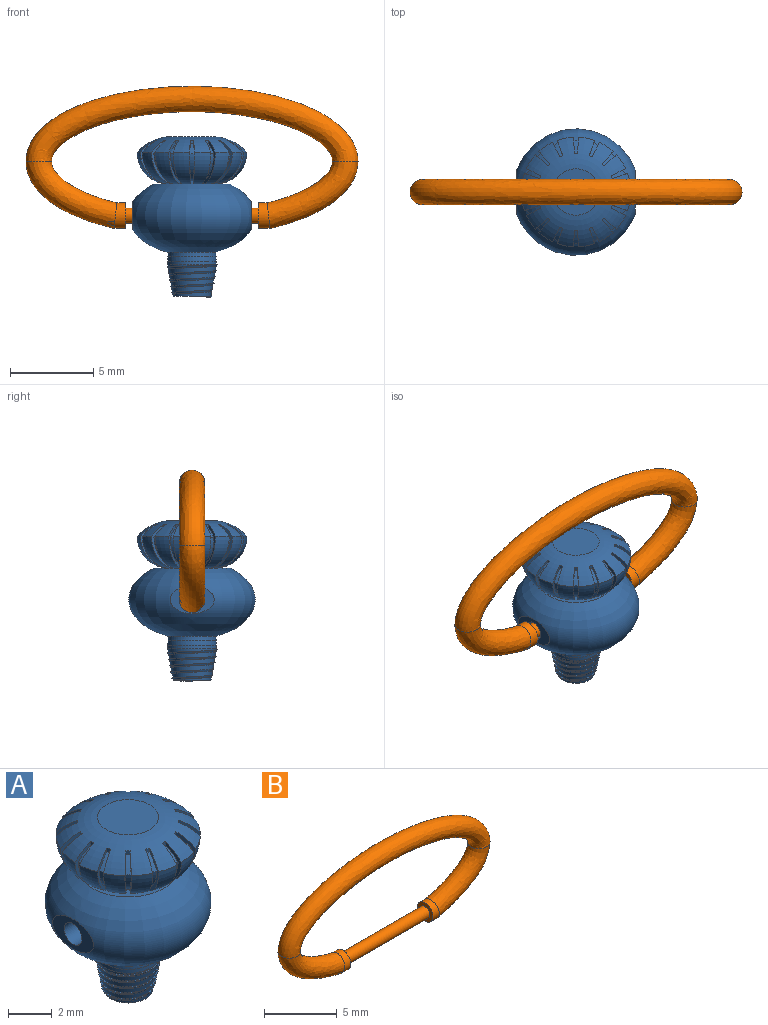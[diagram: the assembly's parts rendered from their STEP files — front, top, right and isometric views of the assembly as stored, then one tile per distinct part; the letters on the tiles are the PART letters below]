
ASSEMBLY  parts=2 mates=1
PART A: 129 faces, bbox 7.6x7.6x9.7 mm
  f0: cone r=1.13mm half-angle=10deg, axis (0,0,1), area 12.2mm2, adj f1,f3,f124,f125,f126,f127
  f1: cylinder r=1.47mm len=2.93mm, axis (0,0,-1), area 2mm2, adj f0,f4,f126,f127
  f2: revolved ~7.62x7.62mm, area 108mm2, adj f5,f6,f121,f122
  f3: plane 2.27x2.27mm, normal (0,0,-1), area 4mm2, adj f0,f124,f125
  f4: revolved ~2.93x2.93mm, area 2.5mm2, adj f1,f5
  f5: torus R=3.33mm, axis (0,0,1), area 2.3mm2, adj f2,f4
  f6: plane 4.57x4.57mm, normal (0,0,1), area 10.3mm2, adj f2,f7,f12,f14,f19,f21,f26,f28
  f7: torus R=1.4mm, axis (0,0,-1), area 2.4mm2, adj f6,f11,f113,f119
  f8: torus R=1.4mm, axis (0,0,-1), area 0.6mm2, adj f9,f11,f12,f13
  f9: torus R=1.17mm, axis (0,0,-1), area 0.2mm2, adj f8,f10,f11,f13
  f10: cylinder r=2.33mm len=0.21mm, axis (0,0,-1), area 0mm2, adj f9,f11,f13,f113
  f11: plane 2.62x1.79mm, normal (-0.34,0.94,0), area 0.7mm2, adj f7,f8,f9,f10,f12,f113
  f12: cylinder r=1.4mm len=0.19mm, axis (0,0,-1), area 0mm2, adj f6,f8,f11,f13
  f13: plane 2.62x1.73mm, normal (0.42,-0.91,0), area 0.7mm2, adj f8,f9,f10,f12,f14,f113
  f14: torus R=1.4mm, axis (0,0,-1), area 2.4mm2, adj f6,f13,f18,f113
  f15: torus R=1.4mm, axis (0,0,-1), area 0.6mm2, adj f16,f18,f19,f20
  f16: torus R=1.17mm, axis (0,0,-1), area 0.2mm2, adj f15,f17,f18,f20
  f17: cylinder r=2.33mm len=0.21mm, axis (0,0,-1), area 0mm2, adj f16,f18,f20,f113
  f18: plane 2.62x1.4mm, normal (-0.68,0.74,0), area 0.7mm2, adj f14,f15,f16,f17,f19,f113
  f19: cylinder r=1.4mm len=0.19mm, axis (0,0,-1), area 0mm2, adj f6,f15,f18,f20
  f20: plane 2.62x1.4mm, normal (0.74,-0.68,0), area 0.7mm2, adj f15,f16,f17,f19,f21,f113
  f21: torus R=1.4mm, axis (0,0,-1), area 2.4mm2, adj f6,f20,f25,f113
  f22: torus R=1.4mm, axis (0,0,-1), area 0.6mm2, adj f23,f25,f26,f27
  f23: torus R=1.17mm, axis (0,0,-1), area 0.2mm2, adj f22,f24,f25,f27
  f24: cylinder r=2.33mm len=0.21mm, axis (0,0,-1), area 0mm2, adj f23,f25,f27,f113
  f25: plane 2.62x1.73mm, normal (-0.91,0.42,0), area 0.7mm2, adj f21,f22,f23,f24,f26,f113
  f26: cylinder r=1.4mm len=0.19mm, axis (0,0,-1), area 0mm2, adj f6,f22,f25,f27
  f27: plane 2.62x1.79mm, normal (0.94,-0.34,0), area 0.7mm2, adj f22,f23,f24,f26,f28,f113
  f28: torus R=1.4mm, axis (0,0,-1), area 2.4mm2, adj f6,f27,f32,f113
  f29: torus R=1.4mm, axis (0,0,-1), area 0.6mm2, adj f30,f32,f33,f34
  f30: torus R=1.17mm, axis (0,0,-1), area 0.2mm2, adj f29,f31,f32,f34
  f31: cylinder r=2.33mm len=0.21mm, axis (0,0,-1), area 0mm2, adj f30,f32,f34,f113
  f32: plane 2.62x1.9mm, normal (-1,0.04,0), area 0.7mm2, adj f28,f29,f30,f31,f33,f113
  f33: cylinder r=1.4mm len=0.19mm, axis (0,0,-1), area 0mm2, adj f6,f29,f32,f34
  f34: plane 2.62x1.9mm, normal (1,0.04,0), area 0.7mm2, adj f29,f30,f31,f33,f35,f113
  f35: torus R=1.4mm, axis (0,0,-1), area 2.4mm2, adj f6,f34,f39,f113
  f36: torus R=1.4mm, axis (0,0,-1), area 0.6mm2, adj f37,f39,f40,f41
  f37: torus R=1.17mm, axis (0,0,-1), area 0.2mm2, adj f36,f38,f39,f41
  f38: cylinder r=2.33mm len=0.21mm, axis (0,0,-1), area 0mm2, adj f37,f39,f41,f113
  f39: plane 2.62x1.79mm, normal (-0.94,-0.34,0), area 0.7mm2, adj f35,f36,f37,f38,f40,f113
  f40: cylinder r=1.4mm len=0.19mm, axis (0,0,-1), area 0mm2, adj f6,f36,f39,f41
  f41: plane 2.62x1.73mm, normal (0.91,0.42,0), area 0.7mm2, adj f36,f37,f38,f40,f42,f113
  f42: torus R=1.4mm, axis (0,0,-1), area 2.4mm2, adj f6,f41,f46,f113
  f43: torus R=1.4mm, axis (0,0,-1), area 0.6mm2, adj f44,f46,f47,f48
  f44: torus R=1.17mm, axis (0,0,-1), area 0.2mm2, adj f43,f45,f46,f48
  f45: cylinder r=2.33mm len=0.21mm, axis (0,0,-1), area 0mm2, adj f44,f46,f48,f113
  f46: plane 2.62x1.4mm, normal (-0.74,-0.68,0), area 0.7mm2, adj f42,f43,f44,f45,f47,f113
  f47: cylinder r=1.4mm len=0.19mm, axis (0,0,-1), area 0mm2, adj f6,f43,f46,f48
  f48: plane 2.62x1.4mm, normal (0.68,0.74,0), area 0.7mm2, adj f43,f44,f45,f47,f49,f113
  f49: torus R=1.4mm, axis (0,0,-1), area 2.4mm2, adj f6,f48,f53,f113
  f50: torus R=1.4mm, axis (0,0,-1), area 0.6mm2, adj f51,f53,f54,f55
  f51: torus R=1.17mm, axis (0,0,-1), area 0.2mm2, adj f50,f52,f53,f55
  f52: cylinder r=2.33mm len=0.21mm, axis (0,0,-1), area 0mm2, adj f51,f53,f55,f113
  f53: plane 2.62x1.73mm, normal (-0.42,-0.91,0), area 0.7mm2, adj f49,f50,f51,f52,f54,f113
  f54: cylinder r=1.4mm len=0.19mm, axis (0,0,-1), area 0mm2, adj f6,f50,f53,f55
  f55: plane 2.62x1.79mm, normal (0.34,0.94,0), area 0.7mm2, adj f50,f51,f52,f54,f56,f113
  f56: torus R=1.4mm, axis (0,0,-1), area 2.4mm2, adj f6,f55,f60,f113
  f57: torus R=1.4mm, axis (0,0,-1), area 0.6mm2, adj f58,f60,f61,f62
  f58: torus R=1.17mm, axis (0,0,-1), area 0.2mm2, adj f57,f59,f60,f62
  f59: cylinder r=2.33mm len=0.21mm, axis (0,0,-1), area 0mm2, adj f58,f60,f62,f113
  f60: plane 2.62x1.9mm, normal (-0.04,-1,0), area 0.7mm2, adj f56,f57,f58,f59,f61,f113
  f61: cylinder r=1.4mm len=0.19mm, axis (0,0,-1), area 0mm2, adj f6,f57,f60,f62
  f62: plane 2.62x1.9mm, normal (-0.04,1,0), area 0.7mm2, adj f57,f58,f59,f61,f63,f113
  f63: torus R=1.4mm, axis (0,0,-1), area 2.4mm2, adj f6,f62,f67,f113
  f64: torus R=1.4mm, axis (0,0,-1), area 0.6mm2, adj f65,f67,f68,f69
  f65: torus R=1.17mm, axis (0,0,-1), area 0.2mm2, adj f64,f66,f67,f69
  f66: cylinder r=2.33mm len=0.21mm, axis (0,0,-1), area 0mm2, adj f65,f67,f69,f113
  f67: plane 2.62x1.79mm, normal (0.34,-0.94,0), area 0.7mm2, adj f63,f64,f65,f66,f68,f113
  f68: cylinder r=1.4mm len=0.19mm, axis (0,0,-1), area 0mm2, adj f6,f64,f67,f69
  f69: plane 2.62x1.73mm, normal (-0.42,0.91,0), area 0.7mm2, adj f64,f65,f66,f68,f70,f113
  f70: torus R=1.4mm, axis (0,0,-1), area 2.4mm2, adj f6,f69,f74,f113
  f71: torus R=1.4mm, axis (0,0,-1), area 0.6mm2, adj f72,f74,f75,f76
  f72: torus R=1.17mm, axis (0,0,-1), area 0.2mm2, adj f71,f73,f74,f76
  f73: cylinder r=2.33mm len=0.21mm, axis (0,0,-1), area 0mm2, adj f72,f74,f76,f113
  f74: plane 2.62x1.4mm, normal (0.68,-0.74,0), area 0.7mm2, adj f70,f71,f72,f73,f75,f113
  f75: cylinder r=1.4mm len=0.19mm, axis (0,0,-1), area 0mm2, adj f6,f71,f74,f76
  f76: plane 2.62x1.4mm, normal (-0.74,0.68,0), area 0.7mm2, adj f71,f72,f73,f75,f77,f113
  f77: torus R=1.4mm, axis (0,0,-1), area 2.4mm2, adj f6,f76,f81,f113
  f78: torus R=1.4mm, axis (0,0,-1), area 0.6mm2, adj f79,f81,f82,f83
  f79: torus R=1.17mm, axis (0,0,-1), area 0.2mm2, adj f78,f80,f81,f83
  f80: cylinder r=2.33mm len=0.21mm, axis (0,0,-1), area 0mm2, adj f79,f81,f83,f113
  f81: plane 2.62x1.73mm, normal (0.91,-0.42,0), area 0.7mm2, adj f77,f78,f79,f80,f82,f113
  f82: cylinder r=1.4mm len=0.19mm, axis (0,0,-1), area 0mm2, adj f6,f78,f81,f83
  f83: plane 2.62x1.79mm, normal (-0.94,0.34,0), area 0.7mm2, adj f78,f79,f80,f82,f84,f113
  f84: torus R=1.4mm, axis (0,0,-1), area 2.4mm2, adj f6,f83,f88,f113
  f85: torus R=1.4mm, axis (0,0,-1), area 0.6mm2, adj f86,f88,f89,f90
  f86: torus R=1.17mm, axis (0,0,-1), area 0.2mm2, adj f85,f87,f88,f90
  f87: cylinder r=2.33mm len=0.21mm, axis (0,0,-1), area 0mm2, adj f86,f88,f90,f113
  f88: plane 2.62x1.9mm, normal (1,-0.04,0), area 0.7mm2, adj f84,f85,f86,f87,f89,f113
  f89: cylinder r=1.4mm len=0.19mm, axis (0,0,-1), area 0mm2, adj f6,f85,f88,f90
  f90: plane 2.62x1.9mm, normal (-1,-0.04,0), area 0.7mm2, adj f85,f86,f87,f89,f91,f113
  f91: torus R=1.4mm, axis (0,0,-1), area 2.4mm2, adj f6,f90,f95,f113
  f92: torus R=1.4mm, axis (0,0,-1), area 0.6mm2, adj f93,f95,f96,f97
  f93: torus R=1.17mm, axis (0,0,-1), area 0.2mm2, adj f92,f94,f95,f97
  f94: cylinder r=2.33mm len=0.21mm, axis (0,0,-1), area 0mm2, adj f93,f95,f97,f113
  f95: plane 2.62x1.79mm, normal (0.94,0.34,0), area 0.7mm2, adj f91,f92,f93,f94,f96,f113
  f96: cylinder r=1.4mm len=0.19mm, axis (0,0,-1), area 0mm2, adj f6,f92,f95,f97
  f97: plane 2.62x1.73mm, normal (-0.91,-0.42,0), area 0.7mm2, adj f92,f93,f94,f96,f98,f113
  f98: torus R=1.4mm, axis (0,0,-1), area 2.4mm2, adj f6,f97,f102,f113
  f99: torus R=1.4mm, axis (0,0,-1), area 0.6mm2, adj f100,f102,f103,f104
  f100: torus R=1.17mm, axis (0,0,-1), area 0.2mm2, adj f99,f101,f102,f104
  f101: cylinder r=2.33mm len=0.21mm, axis (0,0,-1), area 0mm2, adj f100,f102,f104,f113
  f102: plane 2.62x1.4mm, normal (0.74,0.68,0), area 0.7mm2, adj f98,f99,f100,f101,f103,f113
  f103: cylinder r=1.4mm len=0.19mm, axis (0,0,-1), area 0mm2, adj f6,f99,f102,f104
  f104: plane 2.62x1.4mm, normal (-0.68,-0.74,0), area 0.7mm2, adj f99,f100,f101,f103,f105,f113
  f105: torus R=1.4mm, axis (0,0,-1), area 2.4mm2, adj f6,f104,f109,f113
  f106: torus R=1.4mm, axis (0,0,-1), area 0.6mm2, adj f107,f109,f110,f111
  f107: torus R=1.17mm, axis (0,0,-1), area 0.2mm2, adj f106,f108,f109,f111
  f108: cylinder r=2.33mm len=0.21mm, axis (0,0,-1), area 0mm2, adj f107,f109,f111,f113
  f109: plane 2.62x1.73mm, normal (0.42,0.91,0), area 0.7mm2, adj f105,f106,f107,f108,f110,f113
  f110: cylinder r=1.4mm len=0.19mm, axis (0,0,-1), area 0mm2, adj f6,f106,f109,f111
  f111: plane 2.62x1.79mm, normal (-0.34,-0.94,0), area 0.7mm2, adj f106,f107,f108,f110,f113,f114
  f112: plane 2.8x2.8mm, normal (0,0,1), area 6.1mm2, adj f113
  f113: torus R=1.17mm, axis (0,0,-1), area 28.2mm2, adj f7,f10,f11,f13,f14,f17,f18,f20
  f114: torus R=1.4mm, axis (0,0,-1), area 2.4mm2, adj f6,f111,f113,f120
  f115: torus R=1.4mm, axis (0,0,-1), area 0.6mm2, adj f116,f118,f119,f120
  f116: torus R=1.17mm, axis (0,0,-1), area 0.2mm2, adj f115,f117,f119,f120
  f117: cylinder r=2.33mm len=0.21mm, axis (0,0,-1), area 0mm2, adj f113,f116,f119,f120
  f118: cylinder r=1.4mm len=0.19mm, axis (0,0,-1), area 0mm2, adj f6,f115,f119,f120
  f119: plane 2.62x1.9mm, normal (0.04,-1,0), area 0.7mm2, adj f7,f113,f115,f116,f117,f118
  f120: plane 2.62x1.9mm, normal (0.04,1,0), area 0.7mm2, adj f113,f114,f115,f116,f117,f118
  f121: plane 2.66x1.66mm, normal (1,0,0), area 2.4mm2, adj f2,f123
  f122: plane 2.66x1.66mm, normal (-1,0,0), area 2.4mm2, adj f2,f123
  f123: cylinder r=0.57mm len=7.14mm, axis (1,0,0), area 25.6mm2, adj f121,f122
  f124: plane 0.11x0.11mm, normal (-0.01,-1,-0.05), area 0mm2, adj f0,f3,f125,f126,f128
  f125: bspline ~2.89x2.77mm, area 0.8mm2, adj f0,f3,f124,f127,f128
  f126: bspline ~3.03x2.9mm, area 2.5mm2, adj f0,f1,f124,f127,f128
  f127: plane 0.11x0.08mm, normal (0.01,1,0.05), area 0mm2, adj f0,f1,f125,f126,f128
  f128: bspline ~3.03x2.9mm, area 5.5mm2, adj f124,f125,f126,f127
PART B: 8 faces, bbox 20x3.1x8.6 mm
  f0: plane 1.54x1.54mm, normal (-1,0,0), area 1.2mm2, adj f2,f7
  f1: plane 1.54x1.54mm, normal (1,0,0), area 1.2mm2, adj f6,f7
  f2: cylinder r=0.77mm len=1.54mm, axis (-1,0,0), area 3.1mm2, adj f0,f3
  f3: bspline ~5.79x4.06mm, area 29.1mm2, adj f2,f4
  f4: bspline ~19.97x4.53mm, area 102.9mm2, adj f3,f5
  f5: bspline ~5.79x4.06mm, area 29.1mm2, adj f4,f6
  f6: cylinder r=0.77mm len=1.54mm, axis (-1,0,0), area 3.1mm2, adj f1,f5
  f7: cylinder r=0.46mm len=7.99mm, axis (-1,0,0), area 23.1mm2, adj f0,f1
PLACE A t=(2.14,-1.41,-8.58)mm
PLACE B t=(-72.19,6.21,4.04)mm
MATE revolute B.f6 <-> A.f123  axis (-1,0,0) through (-9.26,6.21,12.77)mm
